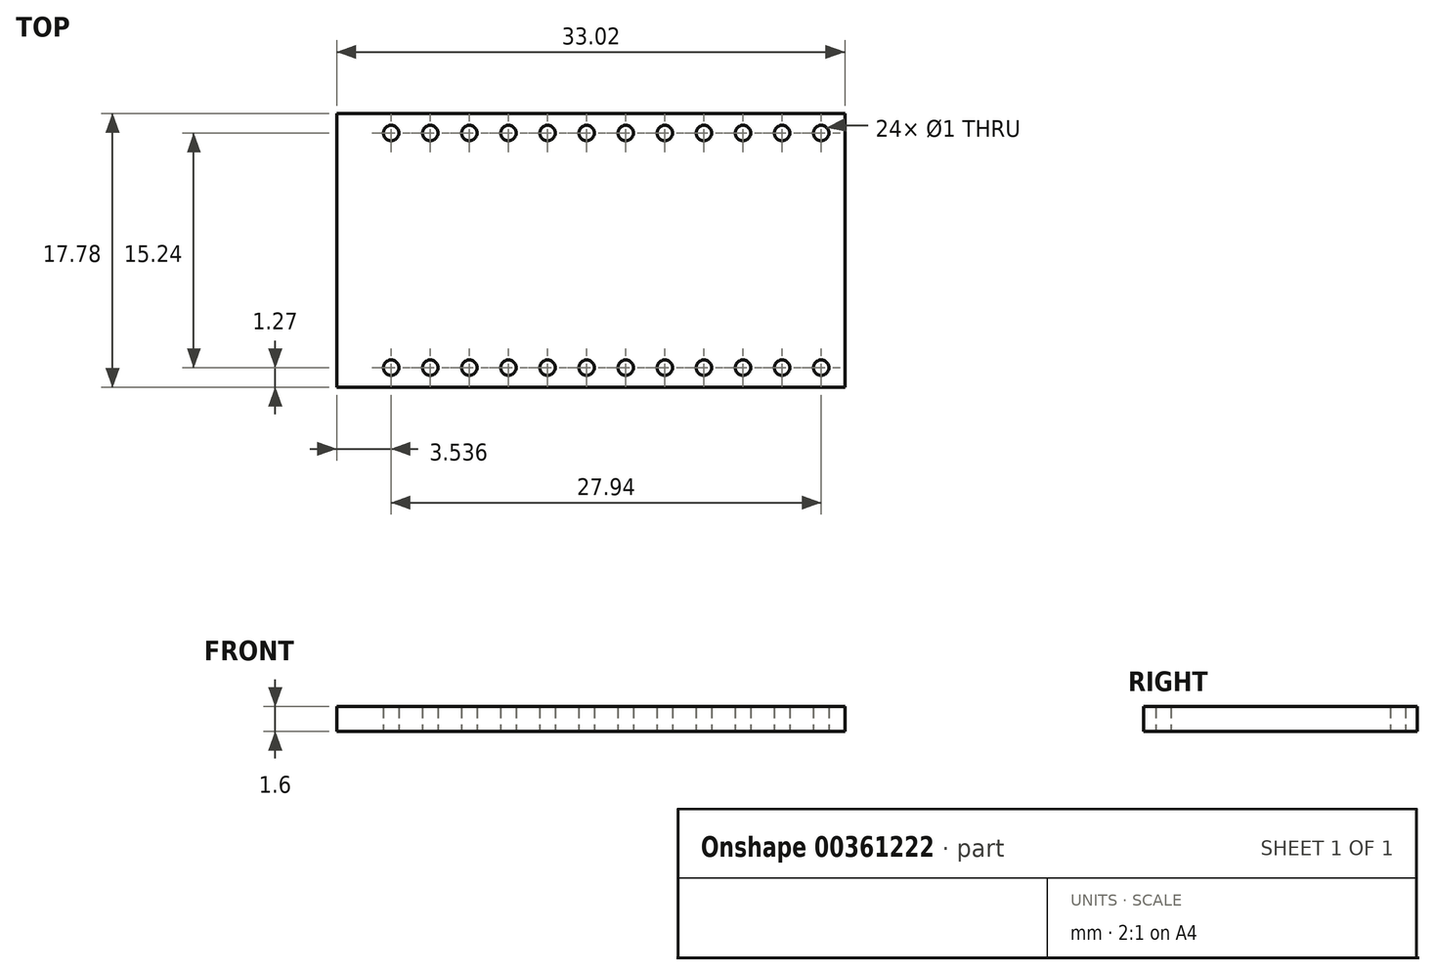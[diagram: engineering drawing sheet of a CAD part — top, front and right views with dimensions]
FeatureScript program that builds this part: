
annotation { "Feature Type Name" : "Feature", "Feature Type Description" : "" }
export const myFeature = defineFeature(function(context is Context, id is Id, definition is map)
    precondition{}
    {
        {
            var Q0;
            Q0=qCreatedBy(makeId("Top.planeOp"),FACE);
            var sketch = newSketch(context, id + "F0", { "sketchPlane" : qUnion([Q0])});
            skLineSegment(sketch, "E0.bottom", {"start": v(16.51, 8.89) * mm, "end": v(-16.51, 8.89) * mm});
            skLineSegment(sketch, "E0.top", {"start": v(16.51, -8.9) * mm, "end": v(-16.51, -8.9) * mm});
            skLineSegment(sketch, "E0.left", {"start": v(16.51, 8.89) * mm, "end": v(16.51, -8.9) * mm});
            skLineSegment(sketch, "E0.right", {"start": v(-16.51, 8.89) * mm, "end": v(-16.51, -8.9) * mm});
            skPoint(sketch, "E0.middle", {"position": v(0, 0) * mm});
            skSolve(sketch);
        }
        {
            var Q0;
            Q0=qSketchRegion(id+"F0",true);
            extrude(context, id + "F1", {"entities" : qUnion([Q0]), "depth" : 1.6 * mm});
        }
        {
            var Q0;
            Q0=qCreatedBy(makeId("Top.planeOp"),FACE);
            var sketch = newSketch(context, id + "F2", { "sketchPlane" : qUnion([Q0])});
            skLineSegment(sketch, "E1", {"start": v(-6.67, 0) * mm, "end": v(-21.2, 0) * mm});
            skCircle(sketch, "E2", {"center": v(-12.97, 7.62) * mm, "radius": 0.5 * mm});
            skCircle(sketch, "E3.1.0.0", {"center": v(-10.43, 7.62) * mm, "radius": 0.5 * mm});
            skCircle(sketch, "E3.2.0.0", {"center": v(-7.9, 7.62) * mm, "radius": 0.5 * mm});
            skCircle(sketch, "E3.3.0.0", {"center": v(-5.35, 7.62) * mm, "radius": 0.5 * mm});
            skCircle(sketch, "E3.4.0.0", {"center": v(-2.81, 7.62) * mm, "radius": 0.5 * mm});
            skCircle(sketch, "E3.5.0.0", {"center": v(-0.27, 7.62) * mm, "radius": 0.5 * mm});
            skCircle(sketch, "E3.6.0.0", {"center": v(2.27, 7.62) * mm, "radius": 0.5 * mm});
            skCircle(sketch, "E3.7.0.0", {"center": v(4.8, 7.62) * mm, "radius": 0.5 * mm});
            skCircle(sketch, "E3.8.0.0", {"center": v(7.35, 7.62) * mm, "radius": 0.5 * mm});
            skCircle(sketch, "E3.9.0.0", {"center": v(9.89, 7.62) * mm, "radius": 0.5 * mm});
            skCircle(sketch, "E3.10.0.0", {"center": v(12.43, 7.62) * mm, "radius": 0.5 * mm});
            skCircle(sketch, "E3.11.0.0", {"center": v(14.97, 7.62) * mm, "radius": 0.5 * mm});
            skLineSegment(sketch, "E3.direction1", {"start": v(-12.97, 7.62) * mm, "end": v(-10.43, 7.62) * mm, "construction": true});
            skCircle(sketch, "E4.MirrorC", {"center": v(2.27, -7.62) * mm, "radius": 0.5 * mm});
            skCircle(sketch, "E5.MirrorC", {"center": v(4.8, -7.62) * mm, "radius": 0.5 * mm});
            skCircle(sketch, "E6.MirrorC", {"center": v(7.35, -7.62) * mm, "radius": 0.5 * mm});
            skCircle(sketch, "E7.MirrorC", {"center": v(9.89, -7.62) * mm, "radius": 0.5 * mm});
            skCircle(sketch, "E8.MirrorC", {"center": v(12.43, -7.62) * mm, "radius": 0.5 * mm});
            skCircle(sketch, "E9.MirrorC", {"center": v(-0.27, -7.62) * mm, "radius": 0.5 * mm});
            skCircle(sketch, "E10.MirrorC", {"center": v(14.97, -7.62) * mm, "radius": 0.5 * mm});
            skCircle(sketch, "E11.MirrorC", {"center": v(-2.81, -7.62) * mm, "radius": 0.5 * mm});
            skCircle(sketch, "E12.MirrorC", {"center": v(-7.9, -7.62) * mm, "radius": 0.5 * mm});
            skCircle(sketch, "E13.MirrorC", {"center": v(-12.97, -7.62) * mm, "radius": 0.5 * mm});
            skCircle(sketch, "E14.MirrorC", {"center": v(-5.35, -7.62) * mm, "radius": 0.5 * mm});
            skCircle(sketch, "E15.MirrorC", {"center": v(-10.43, -7.62) * mm, "radius": 0.5 * mm});
            skSolve(sketch);
        }
        {
            var Q0;
            Q0=qSketchRegion(id+"F2",true);
            extrude(context, id + "F3", {"entities" : qUnion([Q0]), "operationType" : NewBodyOperationType.REMOVE, "depth" : 25 * mm});
        }
    });
